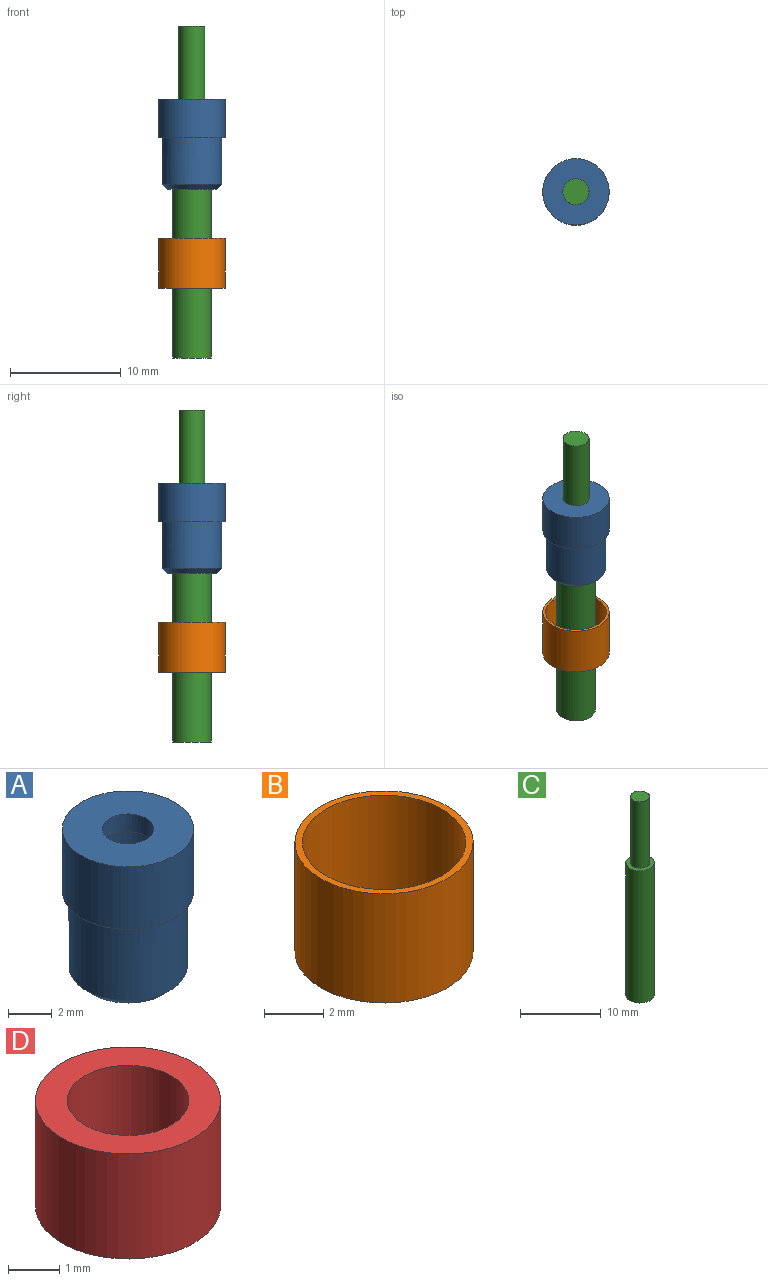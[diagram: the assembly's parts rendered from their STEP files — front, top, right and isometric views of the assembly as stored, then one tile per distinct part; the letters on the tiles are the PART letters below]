
ASSEMBLY  parts=4 mates=4
PART A: 10 faces, bbox 6x6x8.2 mm
  f0: plane 4.5x4.5mm, normal (0,0,-1), area 5.2mm2, adj f5,f7
  f1: plane 3.7x3.7mm, normal (0,0,-1), area 6.4mm2, adj f2,f5
  f2: cylinder r=1.18mm len=2.36mm, axis (0,0,-1), area 7.4mm2, adj f1,f4
  f3: cylinder r=3mm len=6mm, axis (0,0,-1), area 66mm2, adj f4,f6
  f4: plane 6x6mm, normal (0,0,1), area 23.9mm2, adj f2,f3
  f5: cylinder r=1.85mm len=3.7mm, axis (0,0,1), area 29.1mm2, adj f0,f1
  f6: plane 6x6mm, normal (0,0,-1), area 5.4mm2, adj f3,f8
  f7: cylinder r=2.25mm len=4.65mm, axis (0,0,1), area 65.7mm2, adj f0,f9
  f8: cylinder r=2.7mm len=5.4mm, axis (0,0,1), area 71.3mm2, adj f6,f9
  f9: cone r=1.9mm half-angle=45deg, axis (0,0,1), area 9.9mm2, adj f7,f8
PART B: 4 faces, bbox 6x6x4.5 mm
  f0: cylinder r=2.75mm len=5.5mm, axis (0,0,-1), area 77.8mm2, adj f2,f3
  f1: cylinder r=3mm len=6mm, axis (0,0,-1), area 84.8mm2, adj f2,f3
  f2: plane 6x6mm, normal (0,0,1), area 4.5mm2, adj f0,f1
  f3: plane 6x6mm, normal (0,0,-1), area 4.5mm2, adj f0,f1
PART C: 5 faces, bbox 3.5x3.5x30 mm
  f0: cylinder r=1.18mm len=10mm, axis (0,0,-1), area 73.8mm2, adj f1,f4
  f1: plane 2.35x2.35mm, normal (0,0,1), area 4.3mm2, adj f0
  f2: cylinder r=1.75mm len=20mm, axis (0,0,1), area 219.9mm2, adj f3,f4
  f3: plane 3.5x3.5mm, normal (0,0,-1), area 9.6mm2, adj f2
  f4: plane 3.5x3.5mm, normal (0,0,1), area 5.3mm2, adj f0,f2
PART D: 4 faces, bbox 3.6x3.6x2.5 mm
  f0: cylinder r=1.18mm len=2.5mm, axis (0,0,-1), area 18.5mm2, adj f2,f3
  f1: cylinder r=1.8mm len=3.6mm, axis (0,0,-1), area 28.3mm2, adj f2,f3
  f2: plane 3.6x3.6mm, normal (0,0,1), area 5.8mm2, adj f0,f1
  f3: plane 3.6x3.6mm, normal (0,0,-1), area 5.8mm2, adj f0,f1
PLACE A t=(1,2.25,8.4)mm
PLACE B t=(1,2.25,-7.7)mm
PLACE C t=(1,2.25,5.99)mm
PLACE D t=(1,2.25,5.9)mm
MATE planar A.f7 <-> D.f1  axis (0,0,-1) through (1,2.25,8.4)mm
MATE slider B.f0 <-> A.f8  axis (0,0,-1) through (1,2.25,-3.2)mm
MATE slider D.f0 <-> C.f0  axis (0,0,-1) through (1,2.25,7.15)mm
MATE cylindrical A.f5 <-> D.f1  axis (0,0,1) through (1,2.25,7.15)mm
